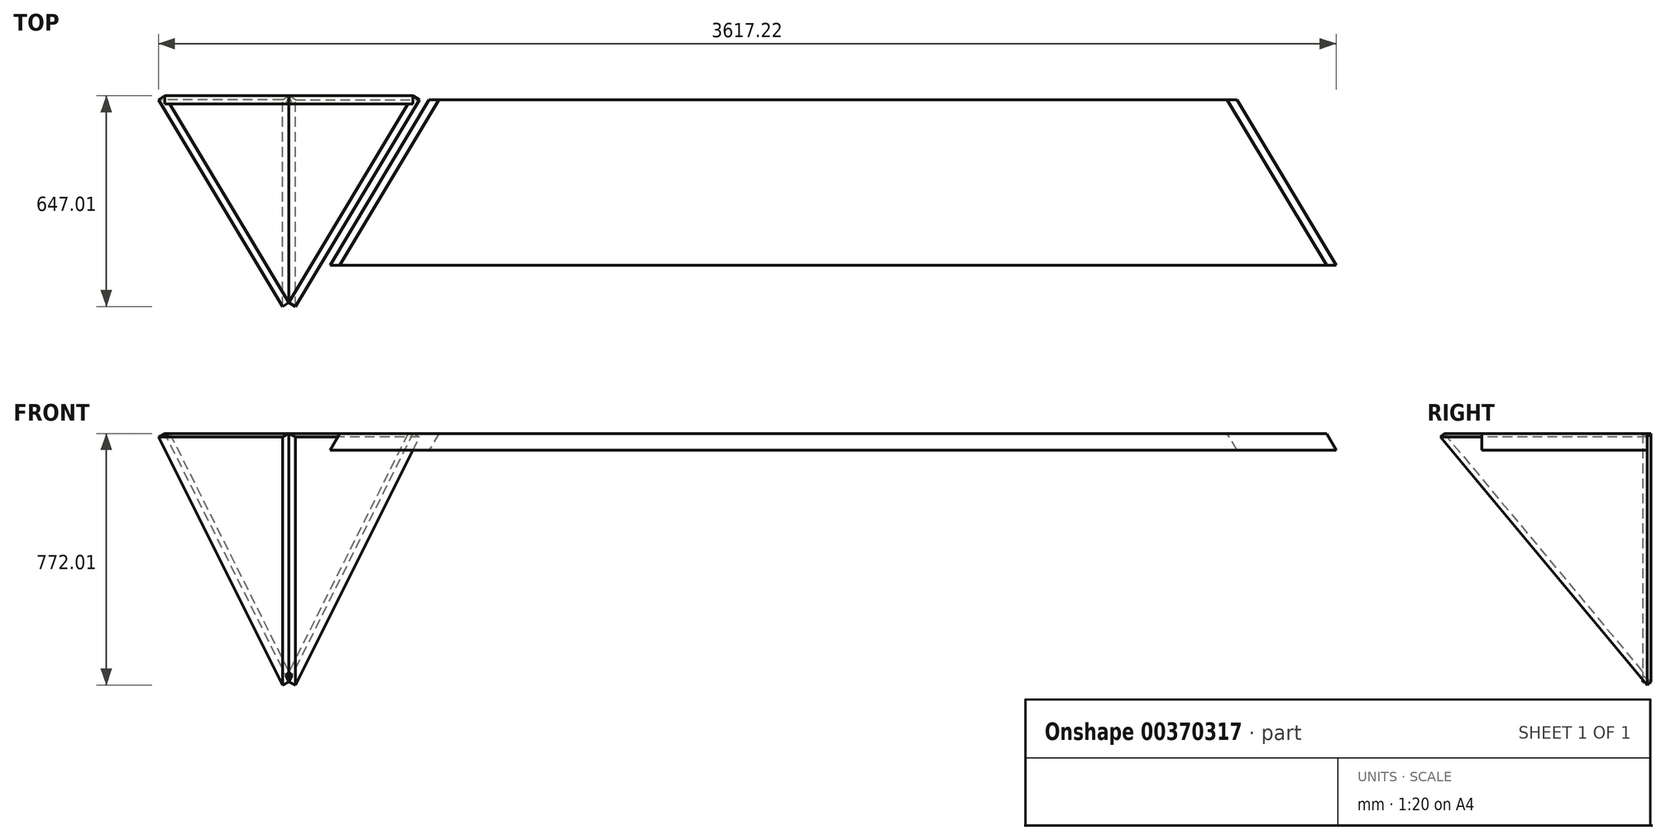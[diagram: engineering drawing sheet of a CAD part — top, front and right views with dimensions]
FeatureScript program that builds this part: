
annotation { "Feature Type Name" : "Feature", "Feature Type Description" : "" }
export const myFeature = defineFeature(function(context is Context, id is Id, definition is map)
    precondition{}
    {
        {
            var Q0;
            Q0=qCreatedBy(makeId("Top.planeOp"),FACE);
            var sketch = newSketch(context, id + "F0", { "sketchPlane" : qUnion([Q0])});
            skLineSegment(sketch, "E0", {"start": v(0, 0) * mm, "end": v(381, 0) * mm});
            skLineSegment(sketch, "E1", {"start": v(381, 0) * mm, "end": v(0, -635) * mm});
            skLineSegment(sketch, "E2", {"start": v(0, 0) * mm, "end": v(0, -635) * mm, "construction": true});
            skSolve(sketch);
        }
        {
            var Q0;
            Q0=qCreatedBy(makeId("Front.planeOp"),FACE);
            var sketch = newSketch(context, id + "F1", { "sketchPlane" : qUnion([Q0])});
            skLineSegment(sketch, "E3", {"start": v(0, 0) * mm, "end": v(0, -762) * mm});
            skLineSegment(sketch, "E4", {"start": v(0, -762) * mm, "end": v(381, 0) * mm});
            skPoint(sketch, "E5.0", {"position": v(381, 0) * mm});
            skLineSegment(sketch, "E6.0", {"start": v(0, 0) * mm, "end": v(381, 0) * mm});
            skPoint(sketch, "E7", {"position": v(0, -199.74) * mm});
            skSolve(sketch);
        }
        {
            var Q0;
            Q0=sQuery(id+"F0.wireOp",VERTEX,"E2.end");
            var Q1;
            Q1=sQuery(id+"F1.wireOp",VERTEX,"E5.0");
            var Q2;
            Q2=sQuery(id+"F1.wireOp",VERTEX,"E4.start");
            cPlane(context, id + "F2", {"entities" : qUnion([Q0, Q1, Q2]), "cplaneType" : CPlaneType.THREE_POINT, "offset" : 25.4 * mm, "width" : 152.4 * mm, "height" : 152.4 * mm});
        }
        {
            var Q0;
            Q0=qCreatedBy(id+"F2.planeOp",FACE);
            var sketch = newSketch(context, id + "F3", { "sketchPlane" : qUnion([Q0])});
            skPoint(sketch, "E8.0", {"position": v(-559.52, 0) * mm});
            skPoint(sketch, "E9.0", {"position": v(161.14, 170.39) * mm});
            skLineSegment(sketch, "E10.0", {"start": v(161.14, 170.39) * mm, "end": v(-559.52, 0) * mm});
            skLineSegment(sketch, "E11.0", {"start": v(161.14, -681.55) * mm, "end": v(161.14, 170.39) * mm});
            skLineSegment(sketch, "E12", {"start": v(-559.52, 0) * mm, "end": v(161.14, -681.55) * mm});
            skSolve(sketch);
        }
        {
            var Q0;
            Q0=makeQuery(id+"F3.imprint","IMPRINT",FACE,{"disambiguationData":[TD([[makeQuery(id+"F3.imprint","IMPRINT",EDGE,{"derivedFrom":sQuery(id+"F3.wireOp",EDGE,"E10.0")}),1.0]])]});
            extrude(context, id + "F4", {"entities" : qUnion([Q0]), "depth" : 25.4 * mm});
        }
        {
            var Q0;
            Q0=makeQuery(id+"F1.imprint","IMPRINT",FACE,{"disambiguationData":[TD([[makeQuery(id+"F1.imprint","IMPRINT",EDGE,{"derivedFrom":sQuery(id+"F1.wireOp",EDGE,"E3")}),1.0]])]});
            extrude(context, id + "F5", {"entities" : qUnion([Q0]), "operationType" : NewBodyOperationType.ADD, "depth" : 25.4 * mm});
        }
        {
            var Q0;
            Q0=makeQuery(id+"F4.opExtrude","SWEPT_BODY",BODY,{"disambiguationData":[OSD([sQuery(id+"F3.wireOp",EDGE,"E10.0"),sQuery(id+"F3.wireOp",EDGE,"E11.0"),sQuery(id+"F3.wireOp",EDGE,"E12")])]});
            var Q1;
            Q1=qCreatedBy(makeId("Right.planeOp"),FACE);
            mirror(context, id + "F6", {"entities" : qUnion([Q0]), "mirrorPlane" : qUnion([Q1])});
        }
        {
            var Q0;
            Q0=qCreatedBy(makeId("Top.planeOp"),FACE);
            var sketch = newSketch(context, id + "F7", { "sketchPlane" : qUnion([Q0])});
            skLineSegment(sketch, "E13", {"start": v(401.02, -12.01) * mm, "end": v(401.02, -520.01) * mm, "construction": true});
            skLineSegment(sketch, "E14", {"start": v(401.02, -12.01) * mm, "end": v(2941.02, -12.01) * mm});
            skLineSegment(sketch, "E15", {"start": v(401.02, -520.01) * mm, "end": v(96.22, -520.01) * mm});
            skLineSegment(sketch, "E16", {"start": v(96.22, -520.01) * mm, "end": v(401.02, -520.01) * mm});
            skLineSegment(sketch, "E17", {"start": v(2941.02, -520.01) * mm, "end": v(401.02, -520.01) * mm});
            skLineSegment(sketch, "E18.0", {"start": v(401.02, -12.01) * mm, "end": v(20.02, -647.01) * mm});
            skLineSegment(sketch, "E19", {"start": v(2941.02, -12.01) * mm, "end": v(2941.02, -520.01) * mm, "construction": true});
            skLineSegment(sketch, "E20", {"start": v(2941.02, -520.01) * mm, "end": v(3245.82, -520.01) * mm});
            skLineSegment(sketch, "E21", {"start": v(3245.82, -520.01) * mm, "end": v(2941.02, -12.01) * mm});
            skSolve(sketch);
        }
        {
            var Q0;
            Q0 = qSketchRegion(id + "F7", true);
            extrude(context, id + "F8", {"entities" : qUnion([Q0]), "oppositeDirection" : true, "depth" : 50.8 * mm});
        }
        {
            var Q0;
            Q0=makeQuery(id+"F8.opExtrude","CAP_EDGE",EDGE,{"disambiguationData":[OSD([sQuery(id+"F7.wireOp",EDGE,"E18.0")])],"isStart":true});
            chamfer(context, id + "F9", {"entities" : qUnion([Q0]), "chamferType" : ChamferType.OFFSET_ANGLE, "width" : 50.8 * mm, "oppositeDirection" : false, "angle" : 63.43 * degree, "tangentPropagation" : true});
        }
        {
            var Q0;
            Q0=makeQuery(id+"F8.opExtrude","CAP_EDGE",EDGE,{"disambiguationData":[OSD([sQuery(id+"F7.wireOp",EDGE,"E21")])],"isStart":true});
            chamfer(context, id + "F10", {"entities" : qUnion([Q0]), "chamferType" : ChamferType.OFFSET_ANGLE, "width" : 50.8 * mm, "oppositeDirection" : false, "angle" : 63.43 * degree, "tangentPropagation" : true});
        }
    });
